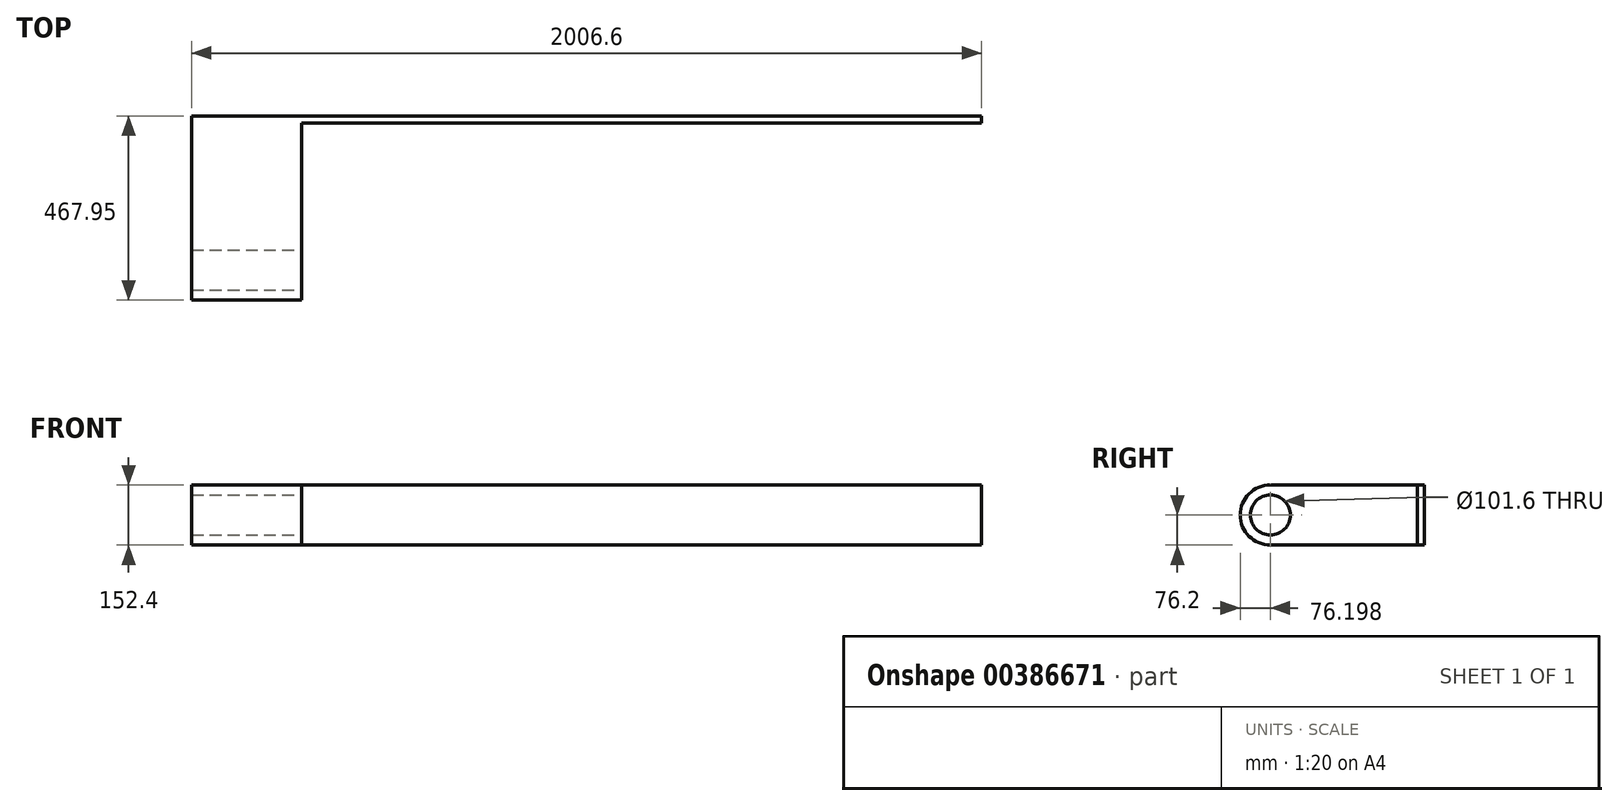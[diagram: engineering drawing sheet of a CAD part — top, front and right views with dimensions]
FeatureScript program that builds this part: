
annotation { "Feature Type Name" : "Feature", "Feature Type Description" : "" }
export const myFeature = defineFeature(function(context is Context, id is Id, definition is map)
    precondition{}
    {
        {
            var Q0;
            Q0=qCreatedBy(makeId("Top.planeOp"),FACE);
            var sketch = newSketch(context, id + "F0", { "sketchPlane" : qUnion([Q0])});
            skLineSegment(sketch, "E0.bottom", {"start": v(-124.64, 201.95) * mm, "end": v(154.76, 201.95) * mm});
            skLineSegment(sketch, "E0.top", {"start": v(-124.64, -128.25) * mm, "end": v(154.76, -128.25) * mm});
            skLineSegment(sketch, "E0.left", {"start": v(-124.64, 201.95) * mm, "end": v(-124.64, -128.25) * mm});
            skLineSegment(sketch, "E0.right", {"start": v(154.76, 201.95) * mm, "end": v(154.76, -128.25) * mm});
            skSolve(sketch);
        }
        {
            var Q0;
            Q0=makeQuery(id+"F0.imprint","IMPRINT",FACE,{"disambiguationData":[TD([[makeQuery(id+"F0.imprint","IMPRINT",EDGE,{"derivedFrom":sQuery(id+"F0.wireOp",EDGE,"E0.bottom")}),-1.0]])]});
            extrude(context, id + "F1", {"entities" : qUnion([Q0]), "depth" : 152.4 * mm});
        }
        {
            var Q0;
            Q0=makeQuery(id+"F1.opExtrude","SWEPT_FACE",FACE,{"disambiguationData":[OSD([sQuery(id+"F0.wireOp",EDGE,"E0.right")])]});
            var sketch = newSketch(context, id + "F2", { "sketchPlane" : qUnion([Q0])});
            skLineSegment(sketch, "E1", {"start": v(201.95, 152.4) * mm, "end": v(-128.25, 152.4) * mm});
            skPoint(sketch, "E2", {"position": v(36.85, 152.4) * mm});
            skPoint(sketch, "E3", {"position": v(-52.05, 76.2) * mm});
            skLineSegment(sketch, "E4", {"start": v(-52.05, 76.2) * mm, "end": v(-128.25, 0) * mm});
            skLineSegment(sketch, "E5", {"start": v(-52.05, 76.2) * mm, "end": v(-128.25, 152.4) * mm});
            skLineSegment(sketch, "E6", {"start": v(-128.25, 76.2) * mm, "end": v(-52.05, 76.2) * mm});
            skSolve(sketch);
        }
        {
            var Q0;
            Q0=sQuery(id+"F2.wireOp",VERTEX,"E3");
            var Q1;
            Q1=makeQuery(id+"F1.opExtrude","SWEPT_BODY",BODY,{"disambiguationData":[OSD([sQuery(id+"F0.wireOp",EDGE,"E0.bottom"),sQuery(id+"F0.wireOp",EDGE,"E0.top"),sQuery(id+"F0.wireOp",EDGE,"E0.left"),sQuery(id+"F0.wireOp",EDGE,"E0.right")])]});
            hole(context, id + "F3", {"style" : HoleStyle.SIMPLE, "endStyle" : HoleEndStyle.THROUGH, "holeDiameter" : 101.6 * mm, "isTappedThrough" : true, "tappedDepth" : 12.7 * mm, "tapClearance" : 3, "locations" : qUnion([Q0]), "scope" : qUnion([Q1])});
        }
        {
            var Q0;
            Q0=makeQuery(id+"F1.opExtrude","SWEPT_FACE",FACE,{"disambiguationData":[OSD([sQuery(id+"F0.wireOp",EDGE,"E0.left")])]});
            var sketch = newSketch(context, id + "F4", { "sketchPlane" : qUnion([Q0])});
            skLineSegment(sketch, "E7", {"start": v(52.05, 0) * mm, "end": v(65, 0) * mm});
            skLineSegment(sketch, "E8", {"start": v(128.25, 76.2) * mm, "end": v(128.25, 76.2) * mm});
            skLineSegment(sketch, "E9", {"start": v(65, 152.4) * mm, "end": v(52.05, 152.4) * mm});
            skPoint(sketch, "E10.visualSharp", {"position": v(128.25, 0) * mm});
            skArc(sketch, "E10.filletArc", {"start": v(52.05, 0) * mm, "mid": v(105.93, 22.32) * mm, "end": v(128.25, 76.2) * mm});
            skPoint(sketch, "E11.visualSharp", {"position": v(128.25, 152.4) * mm});
            skArc(sketch, "E11.filletArc", {"start": v(128.25, 76.2) * mm, "mid": v(105.93, 130.08) * mm, "end": v(52.05, 152.4) * mm});
            skSolve(sketch);
        }
        {
            var Q0;
            {var subQ0=sQuery(id+"F4.wireOp",EDGE,"E7");Q0=makeQuery(id+"F4.imprint","IMPRINT",FACE,{"disambiguationData":[TD([[makeQuery(id+"F4.imprint","IMPRINT",EDGE,{"derivedFrom":subQ0}),1.0]])]});}
            var Q1;
            {var subQ0=sQuery(id+"F4.wireOp",EDGE,"E9");Q1=makeQuery(id+"F4.imprint","IMPRINT",FACE,{"disambiguationData":[TD([[makeQuery(id+"F4.imprint","IMPRINT",EDGE,{"derivedFrom":subQ0}),-1.0]])]});}
            extrude(context, id + "F5", {"entities" : qUnion([Q0, Q1]), "operationType" : NewBodyOperationType.REMOVE, "oppositeDirection" : true, "depth" : 279.4 * mm});
        }
        {
            var Q0;
            Q0=makeQuery(id+"F1.opExtrude","SWEPT_FACE",FACE,{"disambiguationData":[OSD([sQuery(id+"F0.wireOp",EDGE,"E0.right")])]});
            var sketch = newSketch(context, id + "F6", { "sketchPlane" : qUnion([Q0])});
            skLineSegment(sketch, "E12", {"start": v(201.95, 152.4) * mm, "end": v(322, 152.4) * mm});
            skLineSegment(sketch, "E13", {"start": v(322, 152.4) * mm, "end": v(322, 0) * mm});
            skLineSegment(sketch, "E14", {"start": v(322, 0) * mm, "end": v(201.95, 0) * mm});
            skSolve(sketch);
        }
        {
            var Q0;
            Q0=makeQuery(id+"F1.opExtrude","SWEPT_FACE",FACE,{"disambiguationData":[OSD([sQuery(id+"F0.wireOp",EDGE,"E0.bottom")])]});
            extrude(context, id + "F7", {"entities" : qUnion([Q0]), "operationType" : NewBodyOperationType.ADD, "depth" : 137.75 * mm});
        }
        {
            var Q0;
            Q0=makeQuery(id+"F6.imprint","IMPRINT",FACE,{"disambiguationData":[TD([[makeQuery(id+"F6.imprint","IMPRINT",EDGE,{"derivedFrom":sQuery(id+"F6.wireOp",EDGE,"E12")}),-1.0]])]});
            var sketch = newSketch(context, id + "F8", { "sketchPlane" : qUnion([Q0])});
            skLineSegment(sketch, "E15", {"start": v(322, 152.4) * mm, "end": v(339.7, 152.4) * mm});
            skLineSegment(sketch, "E16", {"start": v(339.7, 152.4) * mm, "end": v(339.7, 0) * mm});
            skLineSegment(sketch, "E17", {"start": v(339.7, 0) * mm, "end": v(322, 0) * mm});
            skLineSegment(sketch, "E18", {"start": v(322, 0) * mm, "end": v(322, 152.4) * mm});
            skSolve(sketch);
        }
        {
            var Q0;
            Q0=makeQuery(id+"F8.imprint","IMPRINT",FACE,{"disambiguationData":[TD([[makeQuery(id+"F8.imprint","IMPRINT",EDGE,{"derivedFrom":sQuery(id+"F8.wireOp",EDGE,"E15")}),-1.0]])]});
            extrude(context, id + "F9", {"entities" : qUnion([Q0]), "operationType" : NewBodyOperationType.ADD, "depth" : 1397 * mm});
        }
        {
            var Q0;
            Q0=makeQuery(id+"F9.opExtrude","CAP_EDGE",EDGE,{"disambiguationData":[OSD([sQuery(id+"F8.wireOp",EDGE,"E18")])],"isStart":false});
            var Q1;
            Q1=makeQuery(id+"F9.opExtrude","CAP_VERTEX",VERTEX,{"disambiguationData":[OSD([sQuery(id+"F6.wireOp",EDGE,"E14"),sQuery(id+"F8.wireOp",EDGE,"E17"),sQuery(id+"F8.wireOp",EDGE,"E18")])],"isStart":false});
            cPlane(context, id + "F10", {"entities" : qUnion([Q0, Q1]), "cplaneType" : CPlaneType.LINE_POINT, "offset" : 25.4 * mm, "width" : 152.4 * mm, "height" : 152.4 * mm});
        }
        {
            var Q0;
            Q0=makeQuery(id+"F9.opExtrude","CAP_FACE",FACE,{"disambiguationData":[OSD([sQuery(id+"F8.wireOp",EDGE,"E15"),sQuery(id+"F8.wireOp",EDGE,"E16"),sQuery(id+"F8.wireOp",EDGE,"E17"),sQuery(id+"F8.wireOp",EDGE,"E18")])],"isStart":false});
            extrude(context, id + "F11", {"entities" : qUnion([Q0]), "operationType" : NewBodyOperationType.ADD, "depth" : 330.2 * mm});
        }
    });
